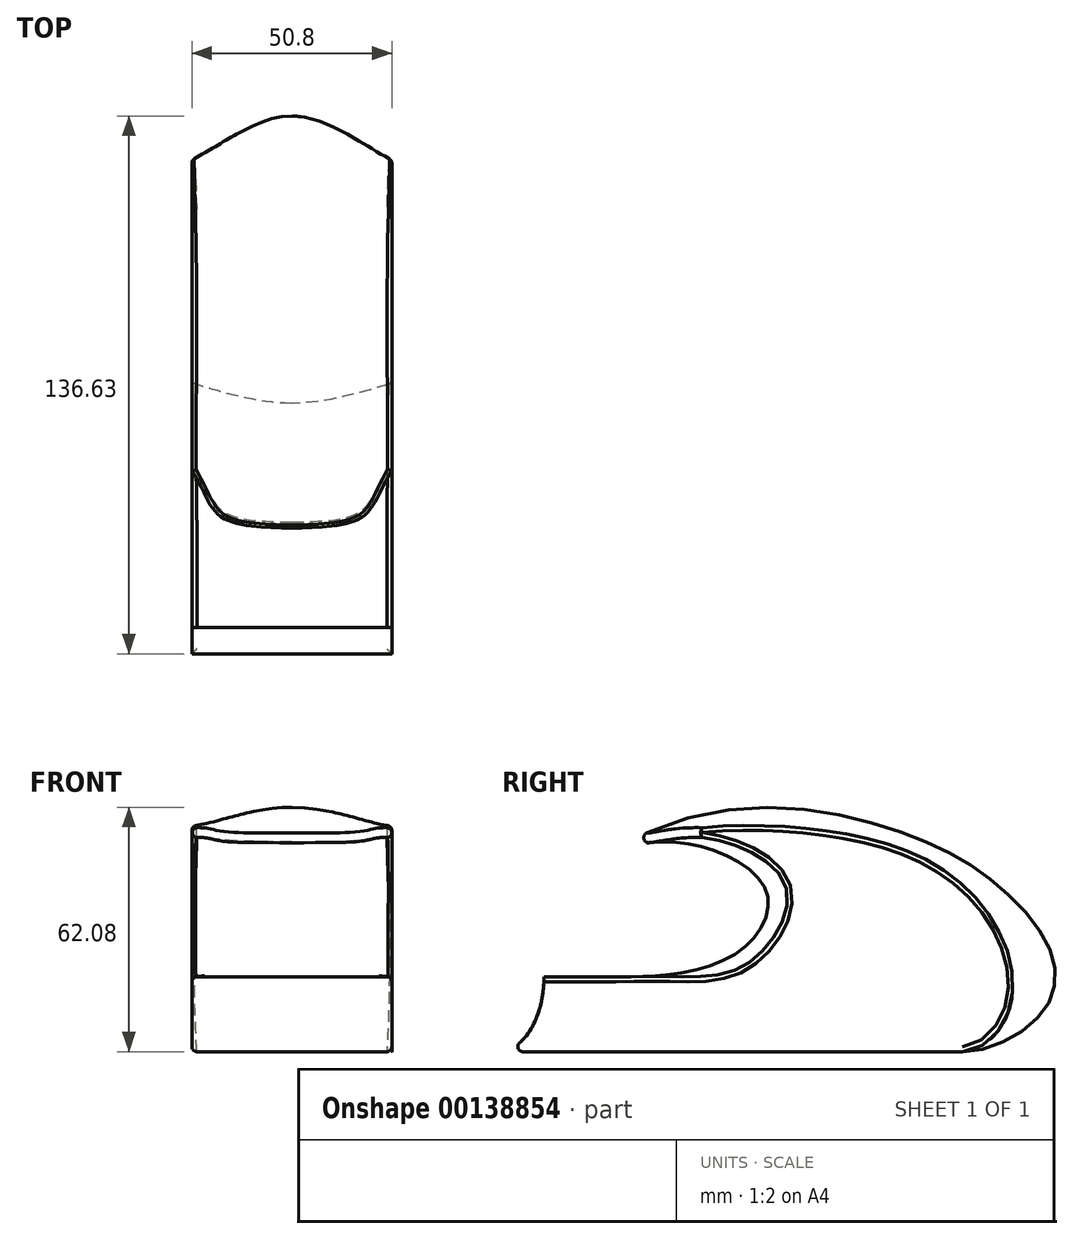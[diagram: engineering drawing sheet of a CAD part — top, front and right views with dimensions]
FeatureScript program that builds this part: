
annotation { "Feature Type Name" : "Feature", "Feature Type Description" : "" }
export const myFeature = defineFeature(function(context is Context, id is Id, definition is map)
    precondition{}
    {
        {
            var Q0;
            Q0=qCreatedBy(makeId("Right.planeOp"),FACE);
            var sketch = newSketch(context, id + "F0", { "sketchPlane" : qUnion([Q0])});
            skLineSegment(sketch, "E0", {"start": v(0, 0) * mm, "end": v(118.04, 0) * mm});
            skFitSpline(sketch, "E1", {"points": [v(118.04, 0) * mm, v(136.92, 8.34) * mm, v(141.32, 22.64) * mm, v(127.03, 42.25) * mm, v(98.98, 56.91) * mm, v(31.53, 52.33) * mm], "startDerivative": vector(116.35, 0) * mm, "endDerivative": vector(-251.55, -142.18) * mm});
            skLineSegment(sketch, "E2.0", {"start": v(11.73, 19.05) * mm, "end": v(33.54, 19.05) * mm});
            skEllipticalArc(sketch, "E3", {});
            skFitSpline(sketch, "E4", {"points": [v(31.53, 52.33) * mm, v(50.77, 52.33) * mm, v(68.19, 40.78) * mm, v(62.14, 26.12) * mm, v(33.54, 19.05) * mm], "startDerivative": vector(77.2, 9.98) * mm, "endDerivative": vector(-110.95, 0) * mm});
            const initialGuessF0  = {"E3": [0, 0.01905, 0, -1, 0.01905, 0.01173123075253416, 0, 1.5707963267948966]};
            skSetInitialGuess(sketch, initialGuessF0);
            skSolve(sketch);
        }
        {
            var Q0;
            Q0=qCreatedBy(makeId("Right.planeOp"),FACE);
            cPlane(context, id + "F1", {"entities" : qUnion([Q0]), "cplaneType" : CPlaneType.OFFSET, "offset" : 25.4 * mm, "width" : 152.4 * mm, "height" : 152.4 * mm});
        }
        {
            var Q0;
            Q0=qCreatedBy(id+"F1.planeOp",FACE);
            var sketch = newSketch(context, id + "F2", { "sketchPlane" : qUnion([Q0])});
            skEllipticalArc(sketch, "E5.0.0", {});
            skLineSegment(sketch, "E5.0.1", {"start": v(0, 0) * mm, "end": v(118.04, 0) * mm});
            skFitSpline(sketch, "E5.0.3", {"points": [v(31.53, 52.33) * mm, v(37.67, 53.13) * mm, v(50.22, 54.77) * mm, v(73.22, 42.65) * mm, v(63.28, 22.04) * mm, v(44.47, 19.05) * mm, v(33.54, 19.05) * mm]});
            skLineSegment(sketch, "E5.0.4", {"start": v(33.54, 19.05) * mm, "end": v(11.73, 19.05) * mm});
            skFitSpline(sketch, "E6", {"points": [v(31.53, 52.33) * mm, v(54.01, 56.91) * mm, v(107.9, 49.03) * mm, v(129.67, 23.33) * mm, v(127.5, 6.3) * mm, v(118.04, 0) * mm], "startDerivative": vector(100.67, 31.02) * mm, "endDerivative": vector(-75.8, 0) * mm});
            const initialGuessF2  = {"E5.0.0": [0, 0.01905, 0, -1, 0.01905, 0.01173123075253416, 0, 1.5707963267948966]};
            skSetInitialGuess(sketch, initialGuessF2);
            skSolve(sketch);
        }
        {
            var Q0;
            Q0=qCreatedBy(makeId("Top.planeOp"),FACE);
            cPlane(context, id + "F3", {"entities" : qUnion([Q0]), "cplaneType" : CPlaneType.OFFSET, "offset" : 25.4 * mm, "width" : 152.4 * mm, "height" : 152.4 * mm});
        }
        {
            var Q0;
            Q0=makeQuery(id+"F0.imprint","IMPRINT",FACE,{"disambiguationData":[TD([[makeQuery(id+"F0.imprint","IMPRINT",EDGE,{"derivedFrom":sQuery(id+"F0.wireOp",EDGE,"E0")}),1.0]])]});
            var Q1;
            Q1=makeQuery(id+"F2.imprint","IMPRINT",FACE,{"disambiguationData":[TD([[makeQuery(id+"F2.imprint","IMPRINT",EDGE,{"derivedFrom":sQuery(id+"F2.wireOp",EDGE,"E5.0.0")}),-1.0]])]});
            loft(context, id + "F4", {"startCondition" : LoftEndDerivativeType.NORMAL_TO_PROFILE, "startMagnitude" : 1, "sheetProfilesArray" : [{ "sheetProfileEntities" : qUnion([Q0]) }, { "sheetProfileEntities" : qUnion([Q1]) }]});
        }
        {
            var Q0;
            Q0=makeQuery(id+"F4.opLoft","SWEPT_BODY",BODY,{"disambiguationData":[OSD([makeQuery(id+"F0.imprint","IMPRINT",FACE,{"disambiguationData":[TD([[makeQuery(id+"F0.imprint","IMPRINT",EDGE,{"derivedFrom":sQuery(id+"F0.wireOp",EDGE,"E0")}),1.0]])]}),makeQuery(id+"F2.imprint","IMPRINT",FACE,{"disambiguationData":[TD([[makeQuery(id+"F2.imprint","IMPRINT",EDGE,{"derivedFrom":sQuery(id+"F2.wireOp",EDGE,"E5.0.0")}),-1.0]])]})])]});
            var Q1;
            Q1=qCreatedBy(makeId("Right.planeOp"),FACE);
            mirror(context, id + "F5", {"operationType" : NewBodyOperationType.ADD, "entities" : qUnion([Q0]), "mirrorPlane" : qUnion([Q1])});
        }
        {
            var Q0;
            Q0=makeQuery(id+"F4.opLoft","SWEPT_EDGE",EDGE,{"disambiguationData":[OSD([sQuery(id+"F0.wireOp",EDGE,"E1"),sQuery(id+"F0.wireOp",EDGE,"E4"),sQuery(id+"F2.wireOp",EDGE,"E5.0.3"),sQuery(id+"F2.wireOp",EDGE,"E6")])]});
            var Q1;
            Q1=makeQuery(id+"F4.opLoft","SWEPT_EDGE",EDGE,{"disambiguationData":[OSD([sQuery(id+"F0.wireOp",EDGE,"E0"),sQuery(id+"F0.wireOp",EDGE,"E3"),sQuery(id+"F2.wireOp",EDGE,"E5.0.0"),sQuery(id+"F2.wireOp",EDGE,"E5.0.1")])]});
            var Q2;
            Q2=makeQuery(id+"F4.opLoft","MID_CAP_EDGE",EDGE,{"disambiguationData":[OSD([sQuery(id+"F2.wireOp",EDGE,"E5.0.0"),sQuery(id+"F2.wireOp",EDGE,"E5.0.3"),sQuery(id+"F2.wireOp",EDGE,"E5.0.4")])],"capPos":1.0});
            var Q3;
            Q3=makeQuery(id+"F5.opPattern","COPY",EDGE,{"derivedFrom":makeQuery(id+"F4.opLoft","MID_CAP_EDGE",EDGE,{"disambiguationData":[OSD([sQuery(id+"F2.wireOp",EDGE,"E5.0.3"),sQuery(id+"F2.wireOp",EDGE,"E5.0.4"),sQuery(id+"F2.wireOp",EDGE,"E6")])],"capPos":1.0}),"instanceName":"1"});
            var Q4;
            Q4=makeQuery(id+"F5.opPattern","COPY",EDGE,{"derivedFrom":makeQuery(id+"F4.opLoft","MID_CAP_EDGE",EDGE,{"disambiguationData":[OSD([sQuery(id+"F2.wireOp",EDGE,"E5.0.1"),sQuery(id+"F2.wireOp",EDGE,"E5.0.3"),sQuery(id+"F2.wireOp",EDGE,"E6")])],"capPos":1.0}),"instanceName":"1"});
            var Q5;
            Q5=makeQuery(id+"F4.opLoft","MID_CAP_EDGE",EDGE,{"disambiguationData":[OSD([sQuery(id+"F2.wireOp",EDGE,"E5.0.1"),sQuery(id+"F2.wireOp",EDGE,"E5.0.3"),sQuery(id+"F2.wireOp",EDGE,"E6")])],"capPos":1.0});
            fillet(context, id + "F6", {"entities" : qUnion([Q0, Q1, Q2, Q3, Q4, Q5]), "radius" : 1.27 * mm, "tangentPropagation" : true, "allowEdgeOverflow" : false});
        }
    });
